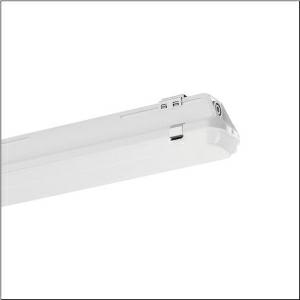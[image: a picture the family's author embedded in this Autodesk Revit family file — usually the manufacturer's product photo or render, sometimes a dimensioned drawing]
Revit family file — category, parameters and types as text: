
# Revit family: monsun_r__12_emergency_51fp10dp467h3h_ce9c
name_source: partatom
category: Lighting Fixtures
units: mm (PartAtom-declared; Revit-internal decimal feet)

## family parameters
Cut with Voids When Loaded = No
Host = Face
Light Source = No
Part Type = Normal
Room Calculation Point = No
Round Connector Dimension = Use Diameter
Shared = No

## types (1)
- --- (1 x LED, 870 lm, 5 W, 4000K)
    Apparent Load = 5 VA
    CIE Flux Codes = 47 77 93 94 100
    Color Rendering = 80
    Color Temperature = 4000K
    Default Elevation = 1800 mm
    Description = Monsun® 12 emergency, damp-proof luminaire, chain hanger, primary optical cover: enclosure, of PMMA, light emission: direct distribution, primary light characteristic: symmetric, installation type: suspended mounting, surface-mounted, horizontal mounting, vertical mounting, LED rated luminous flux: 6.050 lm, light colour: 840, colour temperature: 4000K, control gear: ECG DALI, with terminal, 5+3-pole, max. 2.5mm², mains connection: 220..240V, AC, 50/60Hz, rated input power: 35W, control gear: single battery element, battery: NiCd, 4,5 Ah, mains connection: 230V, 50Hz, luminaire housing, of glass-fibre reinforced polyester, uncoated, bright grey, length: 1.590 mm, width: 90 mm, height: 88mm, clip for enclosure, of stainless steel (V2A), ceiling mounting element, of stainless steel (V2A), chain hanger, of stainless steel (V2A), protection rating (complete): IP66, insulation class (complete): insulation class I (protective earthing), certification: CE, protection symbol: D, impact resistance: IK04, permissible ambient temperature for indoor applications: +5..+35°C, standard: EN 50419, EN 60598-2-1, EN 60598-2-22, no direct snow, no direct sun, no direct rain, for indoor or canopied outdoor use, corresponds to IFS (International Featured Standards) requirements for safety and quality in the food industry, packaging unit: 1 piece
    Height = 89 mm
    Lamp = 1 x LED
    Lamp Light Flux = 870 lm
    Lamp Power = 5 W
    Lamp count = 1
    Length = 1590 mm
    Luminous efficacy = 174 lm/W
    Manufacturer = Siteco
    ModVariant = No
    Model = 51FP10DP467H3H
    Mounting Place = Ceiling
    Mounting Type = Pendant
    Number of Poles = 1
    OnlyDefault = Yes
    Power Factor = 1
    Product Name = Monsun® 12 emergency
    Product group = damp-proof luminaire | ceiling pendant
    ProductGroupID = 908
    Protection Class = Protection class I
    Protection Degree = IP 66
    RLX_Detail_Level = 1
    RlxData = <blob elided: 92065 chars, md5=cf79b3e2>
    Socket = socket
    Standby Power = 0 W
    System Light Flux = 870 lm
    System Power = 5 W
    Type Comments = : emergency light operation: 3 h
    Type Image = l_1004748.jpg
    URL = http://relux.com
    VarID = @adj_125639
    Voltage = 0 V
    Weight = 0.00 kg
    Width = 90 mm

## geometry (parser evidence)
native form markers: Blend x4, Sweep x13
no freeform markers — native parametric forms only
